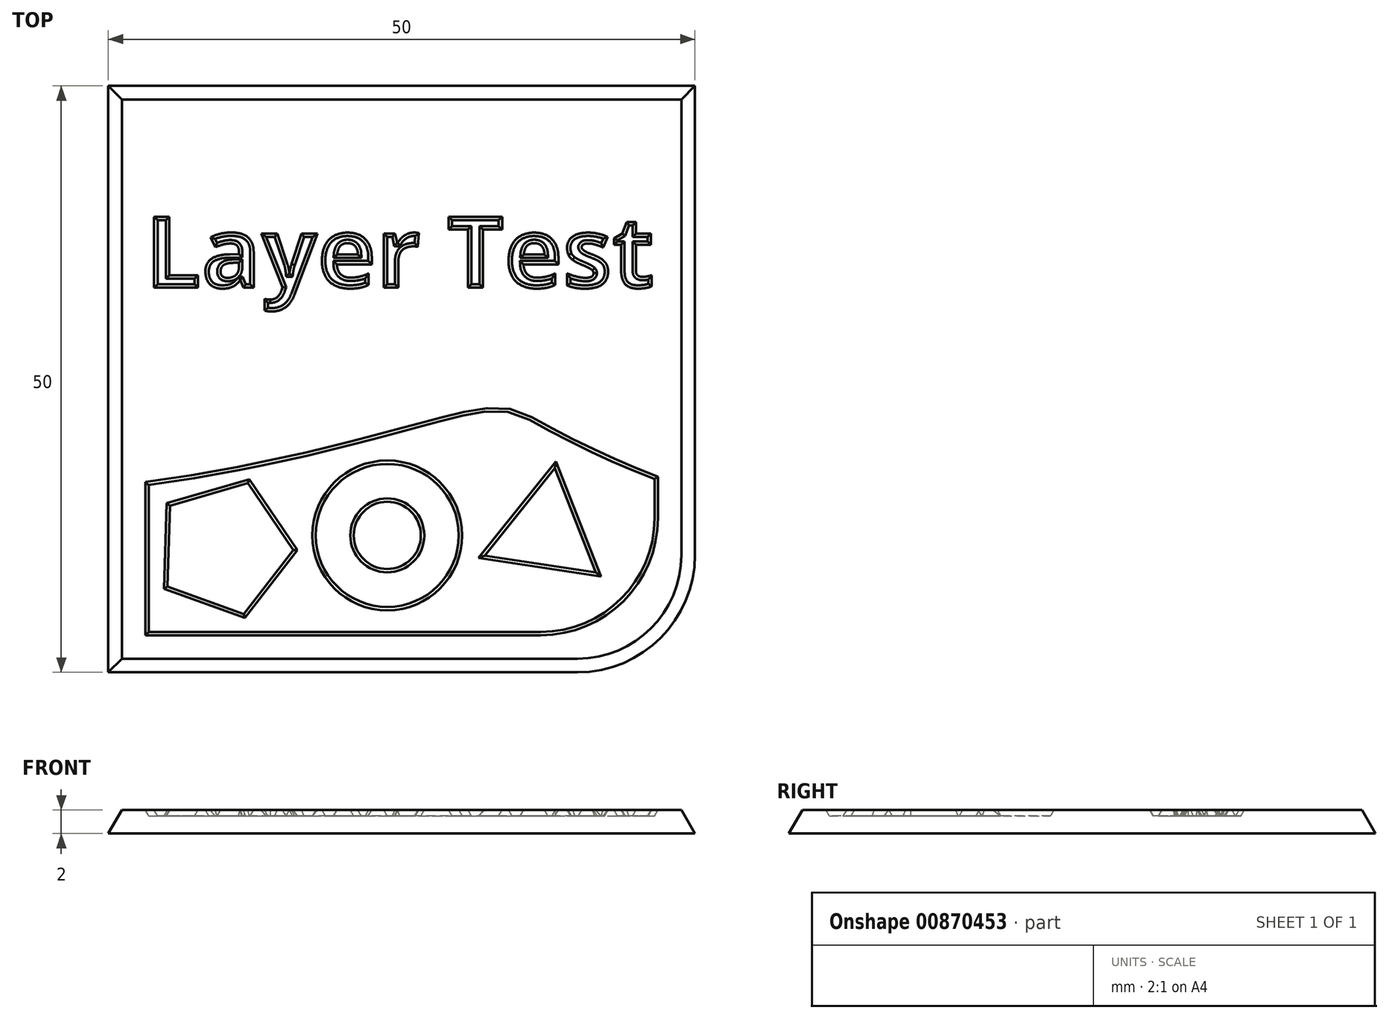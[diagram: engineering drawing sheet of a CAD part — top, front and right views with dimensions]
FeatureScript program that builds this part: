
annotation { "Feature Type Name" : "Feature", "Feature Type Description" : "" }
export const myFeature = defineFeature(function(context is Context, id is Id, definition is map)
    precondition{}
    {
        {
            var Q0;
            Q0=qCreatedBy(makeId("Top.planeOp"),FACE);
            var sketch = newSketch(context, id + "F0", { "sketchPlane" : qUnion([Q0])});
            skLineSegment(sketch, "E0.bottom", {"start": v(25, 25) * mm, "end": v(-25, 25) * mm});
            skLineSegment(sketch, "E0.top", {"start": v(15, -25) * mm, "end": v(-25, -25) * mm});
            skLineSegment(sketch, "E0.left", {"start": v(25, 25) * mm, "end": v(25, -15) * mm});
            skLineSegment(sketch, "E0.right", {"start": v(-25, 25) * mm, "end": v(-25, -25) * mm});
            skPoint(sketch, "E0.middle", {"position": v(0, 0) * mm});
            skPoint(sketch, "E1.visualSharp", {"position": v(25, -25) * mm});
            skArc(sketch, "E1.filletArc", {"start": v(15, -25) * mm, "mid": v(22.07, -22.07) * mm, "end": v(25, -15) * mm});
            skSolve(sketch);
        }
        {
            var Q0;
            Q0=makeQuery(id+"F0.imprint","IMPRINT",FACE,{"disambiguationData":[TD([[makeQuery(id+"F0.imprint","IMPRINT",EDGE,{"derivedFrom":sQuery(id+"F0.wireOp",EDGE,"E0.bottom")}),1.0]])]});
            extrude(context, id + "F1", {"entities" : qUnion([Q0]), "depth" : 2 * mm, "offsetDistance" : 25 * mm, "hasDraft" : true, "draftAngle" : 30 * degree, "draftPullDirection" : true});
        }
        {
            var Q0;
            Q0=makeQuery(id+"F1.opExtrude","CAP_FACE",FACE,{"disambiguationData":[OSD([sQuery(id+"F0.wireOp",EDGE,"E0.bottom"),sQuery(id+"F0.wireOp",EDGE,"E0.top"),sQuery(id+"F0.wireOp",EDGE,"E0.left"),sQuery(id+"F0.wireOp",EDGE,"E0.right")])],"isStart":false});
            var sketch = newSketch(context, id + "F2", { "sketchPlane" : qUnion([Q0])});
            skFitSpline(sketch, "E2", {"points": [v(-21.85, -8.78) * mm, v(8.16, -2.42) * mm, v(21.85, -8.32) * mm], "startDerivative": vector(87.3, 12.22) * mm, "endDerivative": vector(74.16, -28.93) * mm});
            skLineSegment(sketch, "E3.bottom", {"start": v(11.85, -21.85) * mm, "end": v(-21.85, -21.85) * mm, "construction": true});
            skLineSegment(sketch, "E3.top", {"start": v(21.85, 21.85) * mm, "end": v(-21.85, 21.85) * mm, "construction": true});
            skLineSegment(sketch, "E3.left", {"start": v(21.85, -11.85) * mm, "end": v(21.85, 21.85) * mm, "construction": true});
            skLineSegment(sketch, "E3.right", {"start": v(-21.85, -21.85) * mm, "end": v(-21.85, 21.85) * mm, "construction": true});
            skPoint(sketch, "E3.middle", {"position": v(0, 0) * mm});
            skLineSegment(sketch, "E4", {"start": v(-21.85, -8.78) * mm, "end": v(-21.85, -21.85) * mm});
            skLineSegment(sketch, "E5", {"start": v(21.85, -21.85) * mm, "end": v(21.85, -8.32) * mm});
            skLineSegment(sketch, "E6", {"start": v(-21.85, -21.85) * mm, "end": v(21.85, -21.85) * mm});
            skPoint(sketch, "E7.visualSharp", {"position": v(21.85, -21.85) * mm});
            skArc(sketch, "E7.filletArc", {"start": v(11.85, -21.85) * mm, "mid": v(18.92, -18.92) * mm, "end": v(21.85, -11.85) * mm});
            skText(sketch, "E8", { "text": "Layer Test", "fontName": "OpenSans-Bold.ttf"});
            skCircle(sketch, "E9", {"center": v(-1.22, -13.32) * mm, "radius": 6.1 * mm});
            skCircle(sketch, "E10", {"center": v(-1.22, -13.32) * mm, "radius": 3.15 * mm});
            skCircle(sketch, "E11.cCircle", {"center": v(-15.1, -14.4) * mm, "radius": 4.75 * mm, "construction": true});
            skLineSegment(sketch, "E11.0", {"start": v(-9.23, -14.58) * mm, "end": v(-13.46, -20.03) * mm});
            skLineSegment(sketch, "E11.1", {"start": v(-13.46, -20.03) * mm, "end": v(-19.95, -17.69) * mm});
            skLineSegment(sketch, "E11.2", {"start": v(-19.95, -17.69) * mm, "end": v(-19.73, -10.8) * mm});
            skLineSegment(sketch, "E11.3", {"start": v(-19.73, -10.8) * mm, "end": v(-13.11, -8.87) * mm});
            skLineSegment(sketch, "E11.4", {"start": v(-13.11, -8.87) * mm, "end": v(-9.23, -14.58) * mm});
            skPoint(sketch, "E11.0.midPoint", {"position": v(-11.35, -17.3) * mm});
            skCircle(sketch, "E12.cCircle", {"center": v(12.23, -13.03) * mm, "radius": 2.76 * mm, "construction": true});
            skLineSegment(sketch, "E12.0", {"start": v(13.06, -7.58) * mm, "end": v(16.55, -16.48) * mm});
            skLineSegment(sketch, "E12.1", {"start": v(16.55, -16.48) * mm, "end": v(7.1, -15.05) * mm});
            skLineSegment(sketch, "E12.2", {"start": v(7.1, -15.05) * mm, "end": v(13.06, -7.58) * mm});
            skPoint(sketch, "E12.0.midPoint", {"position": v(14.8, -12.03) * mm});
            const initialGuessF2  = {"E8": [-0.02185, 0.0078, 1, 0, 0.00608]};
            skSetInitialGuess(sketch, initialGuessF2);
            skSolve(sketch);
        }
        {
            var Q0;
            Q0=makeQuery(id+"F2.imprint","IMPRINT",FACE,{"disambiguationData":[TD([[makeQuery(id+"F2.imprint","IMPRINT",EDGE,{"derivedFrom":sQuery(id+"F2.wireOp",EDGE,"E2")}),-1.0]])]});
            var Q1;
            Q1=makeQuery(id+"F2.imprint","IMPRINT",FACE,{"disambiguationData":[TD([[makeQuery(id+"F2.imprint","IMPRINT",EDGE,{"derivedFrom":sQuery(id+"F2.wireOp",EDGE,"E8.sketch_text.stroke-0")}),-1.0]])]});
            var Q2;
            Q2=makeQuery(id+"F2.imprint","IMPRINT",FACE,{"disambiguationData":[TD([[makeQuery(id+"F2.imprint","IMPRINT",EDGE,{"derivedFrom":sQuery(id+"F2.wireOp",EDGE,"E8.sketch_text.stroke-6")}),-1.0]])]});
            var Q3;
            Q3=makeQuery(id+"F2.imprint","IMPRINT",FACE,{"disambiguationData":[TD([[makeQuery(id+"F2.imprint","IMPRINT",EDGE,{"derivedFrom":sQuery(id+"F2.wireOp",EDGE,"E8.sketch_text.stroke-31")}),-1.0]])]});
            var Q4;
            Q4=makeQuery(id+"F2.imprint","IMPRINT",FACE,{"disambiguationData":[TD([[makeQuery(id+"F2.imprint","IMPRINT",EDGE,{"derivedFrom":sQuery(id+"F2.wireOp",EDGE,"E8.sketch_text.stroke-48")}),-1.0]])]});
            var Q5;
            Q5=makeQuery(id+"F2.imprint","IMPRINT",FACE,{"disambiguationData":[TD([[makeQuery(id+"F2.imprint","IMPRINT",EDGE,{"derivedFrom":sQuery(id+"F2.wireOp",EDGE,"E8.sketch_text.stroke-68")}),-1.0]])]});
            var Q6;
            Q6=makeQuery(id+"F2.imprint","IMPRINT",FACE,{"disambiguationData":[TD([[makeQuery(id+"F2.imprint","IMPRINT",EDGE,{"derivedFrom":sQuery(id+"F2.wireOp",EDGE,"E8.sketch_text.stroke-81")}),-1.0]])]});
            var Q7;
            Q7=makeQuery(id+"F2.imprint","IMPRINT",FACE,{"disambiguationData":[TD([[makeQuery(id+"F2.imprint","IMPRINT",EDGE,{"derivedFrom":sQuery(id+"F2.wireOp",EDGE,"E8.sketch_text.stroke-89")}),-1.0]])]});
            var Q8;
            Q8=makeQuery(id+"F2.imprint","IMPRINT",FACE,{"disambiguationData":[TD([[makeQuery(id+"F2.imprint","IMPRINT",EDGE,{"derivedFrom":sQuery(id+"F2.wireOp",EDGE,"E8.sketch_text.stroke-109")}),-1.0]])]});
            var Q9;
            Q9=makeQuery(id+"F2.imprint","IMPRINT",FACE,{"disambiguationData":[TD([[makeQuery(id+"F2.imprint","IMPRINT",EDGE,{"derivedFrom":sQuery(id+"F2.wireOp",EDGE,"E8.sketch_text.stroke-135")}),-1.0]])]});
            var Q10;
            Q10=makeQuery(id+"F2.imprint","IMPRINT",FACE,{"disambiguationData":[TD([[makeQuery(id+"F2.imprint","IMPRINT",EDGE,{"derivedFrom":sQuery(id+"F2.wireOp",EDGE,"E10")}),1.0]])]});
            extrude(context, id + "F3", {"entities" : qUnion([Q0, Q1, Q2, Q3, Q4, Q5, Q6, Q7, Q8, Q9, Q10]), "operationType" : NewBodyOperationType.REMOVE, "oppositeDirection" : true, "depth" : .5 * mm, "offsetDistance" : 25 * mm, "hasDraft" : true, "draftAngle" : 30 * degree, "draftPullDirection" : true});
        }
    });
